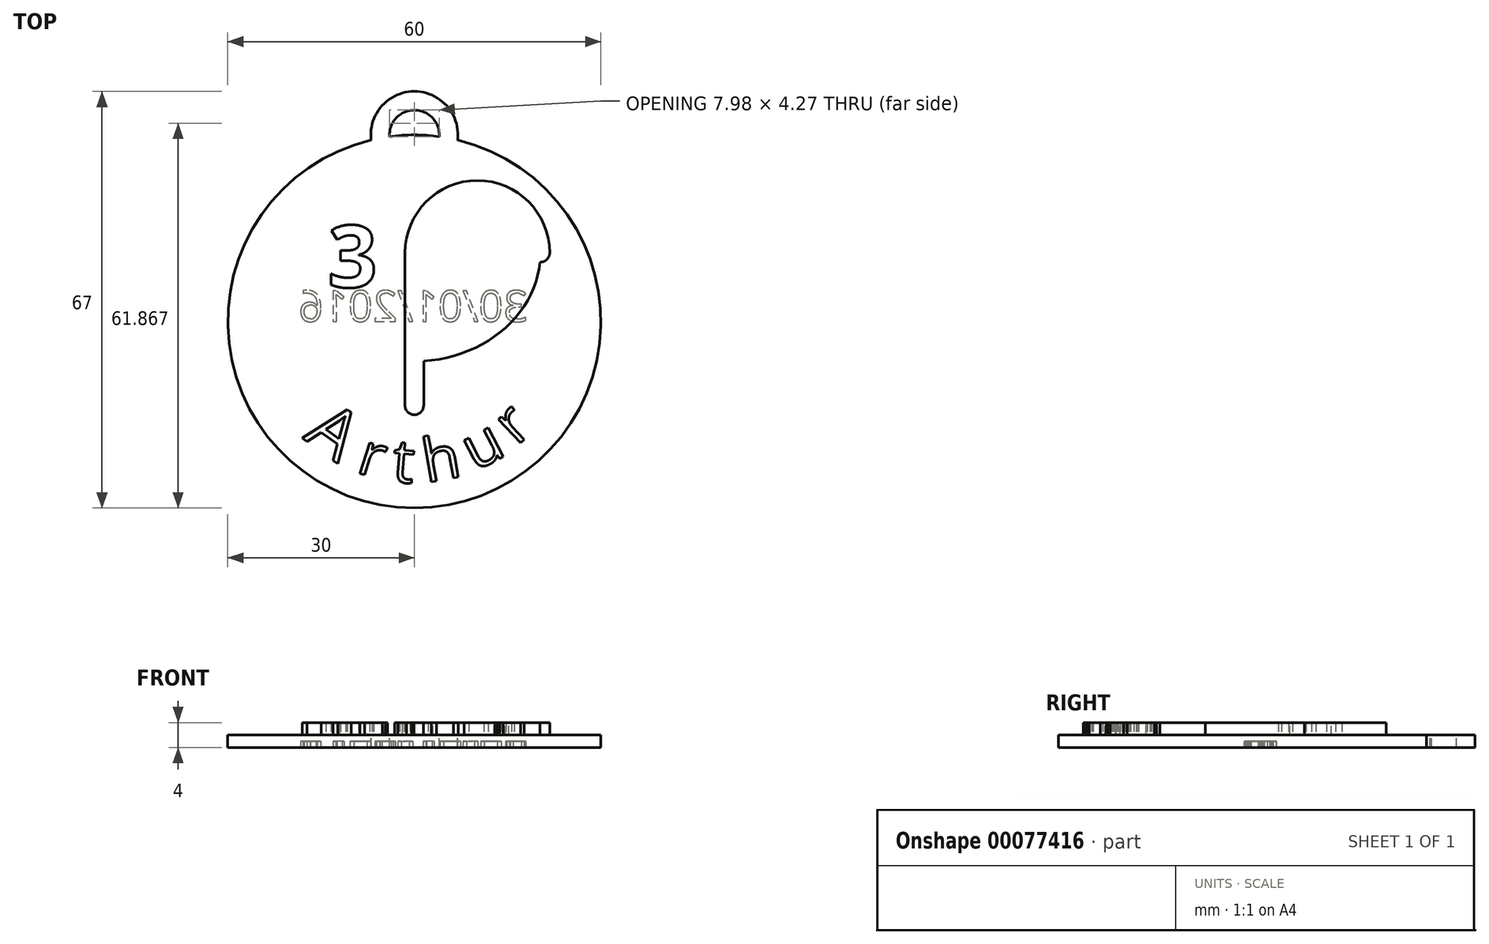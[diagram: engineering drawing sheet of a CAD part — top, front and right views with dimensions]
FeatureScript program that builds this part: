
annotation { "Feature Type Name" : "Feature", "Feature Type Description" : "" }
export const myFeature = defineFeature(function(context is Context, id is Id, definition is map)
    precondition{}
    {
        {
            var Q0;
            Q0=qCreatedBy(makeId("Top.planeOp"),FACE);
            var sketch = newSketch(context, id + "F0", { "sketchPlane" : qUnion([Q0])});
            skCircle(sketch, "E0", {"center": v(0, 0) * mm, "radius": 30 * mm});
            skSolve(sketch);
        }
        {
            var Q0;
            Q0=qSketchRegion(id+"F0",true);
            extrude(context, id + "F1", {"entities" : qUnion([Q0]), "oppositeDirection" : true, "depth" : 2 * mm});
        }
        {
            var Q0;
            Q0=qCreatedBy(makeId("Top.planeOp"),FACE);
            var sketch = newSketch(context, id + "F2", { "sketchPlane" : qUnion([Q0])});
            skEllipticalArc(sketch, "E1", {});
            skLineSegment(sketch, "E2", {"start": v(0, 0) * mm, "end": v(0, 30) * mm, "construction": true});
            skLineSegment(sketch, "E3", {"start": v(0, 11.04) * mm, "end": v(0, -13.5) * mm});
            skArc(sketch, "E4", {"start": v(20.27, 11.04) * mm, "mid": v(10.13, 21.17) * mm, "end": v(0, 11.04) * mm});
            skLineSegment(sketch, "E5", {"start": v(0, 11.04) * mm, "end": v(-16.84, 20.76) * mm, "construction": true});
            skLineSegment(sketch, "E6", {"start": v(0, 11.04) * mm, "end": v(-20.27, 11.04) * mm, "construction": true});
            skArc(sketch, "E7.0.startCap", {"start": v(-1.5, 11.04) * mm, "mid": v(0, 12.54) * mm, "end": v(1.5, 11.04) * mm});
            skArc(sketch, "E7.0.endCap", {"start": v(1.5, -13.5) * mm, "mid": v(0, -15) * mm, "end": v(-1.5, -13.5) * mm});
            skLineSegment(sketch, "E7.0.left", {"start": v(1.5, 11.04) * mm, "end": v(1.5, -13.5) * mm});
            skLineSegment(sketch, "E7.0.right", {"start": v(-1.5, 11.04) * mm, "end": v(-1.5, -13.5) * mm});
            skArc(sketch, "E8.0.startCap", {"start": v(21.77, 11.04) * mm, "mid": v(20.27, 9.54) * mm, "end": v(18.77, 11.04) * mm});
            skArc(sketch, "E8.0.endCap", {"start": v(1.5, 11.04) * mm, "mid": v(0, 9.54) * mm, "end": v(-1.5, 11.04) * mm});
            skArc(sketch, "E8.0.left", {"start": v(18.77, 11.04) * mm, "mid": v(10.13, 19.67) * mm, "end": v(1.5, 11.04) * mm});
            skArc(sketch, "E8.0.right", {"start": v(21.77, 11.04) * mm, "mid": v(10.13, 22.67) * mm, "end": v(-1.5, 11.04) * mm});
            skArc(sketch, "E8.1.startCap", {"start": v(-18.02, 21.68) * mm, "mid": v(-15.91, 21.95) * mm, "end": v(-15.65, 19.84) * mm});
            skArc(sketch, "E8.1.endCap", {"start": v(18.77, 11.04) * mm, "mid": v(20.27, 12.54) * mm, "end": v(21.77, 11.04) * mm});
            skFitSpline(sketch, "E8.1.left", {"points": [v(18.7, 9.5) * mm, v(18.8, 11.04) * mm, v(18.7, 12.6) * mm, v(18.36, 14.63) * mm, v(17.66, 16.6) * mm, v(16.63, 18.49) * mm, v(15.37, 20.3) * mm, v(13.44, 22.32) * mm, v(11.07, 24) * mm, v(8.94, 25.1) * mm, v(6.7, 26.01) * mm, v(4.32, 26.63) * mm, v(1.87, 26.95) * mm, v(0, 27.03) * mm, v(-1.87, 26.95) * mm, v(-4.32, 26.63) * mm, v(-6.7, 26.01) * mm, v(-8.94, 25.1) * mm, v(-11.07, 24) * mm, v(-13.44, 22.32) * mm, v(-15.37, 20.3) * mm, v(-16.63, 18.49) * mm, v(-17.66, 16.6) * mm, v(-18.36, 14.63) * mm, v(-18.7, 12.6) * mm, v(-18.8, 11.04) * mm, v(-18.7, 9.5) * mm, v(-18.36, 7.46) * mm, v(-17.66, 5.48) * mm, v(-16.63, 3.6) * mm, v(-15.37, 1.8) * mm, v(-13.44, -0.24) * mm, v(-11.07, -1.92) * mm, v(-8.94, -3.02) * mm, v(-6.7, -3.93) * mm, v(-4.32, -4.55) * mm, v(-1.87, -4.86) * mm, v(0, -4.94) * mm, v(1.87, -4.86) * mm, v(4.32, -4.55) * mm, v(6.7, -3.93) * mm, v(8.94, -3.02) * mm, v(11.07, -1.92) * mm, v(13.44, -0.24) * mm, v(15.37, 1.8) * mm, v(16.63, 3.6) * mm, v(17.66, 5.48) * mm, v(18.36, 7.46) * mm, v(18.7, 9.5) * mm, v(18.8, 11.04) * mm, v(18.7, 12.6) * mm]});
            skFitSpline(sketch, "E8.1.right", {"points": [v(21.7, 9.15) * mm, v(21.8, 11.04) * mm, v(21.7, 12.93) * mm, v(21.27, 15.42) * mm, v(20.42, 17.81) * mm, v(19.18, 20.07) * mm, v(17.69, 22.22) * mm, v(15.4, 24.61) * mm, v(12.65, 26.56) * mm, v(10.2, 27.83) * mm, v(7.62, 28.88) * mm, v(4.92, 29.58) * mm, v(2.12, 29.94) * mm, v(0, 30.03) * mm, v(-2.12, 29.94) * mm, v(-4.92, 29.58) * mm, v(-7.62, 28.88) * mm, v(-10.2, 27.83) * mm, v(-12.65, 26.56) * mm, v(-15.4, 24.61) * mm, v(-17.69, 22.22) * mm, v(-19.18, 20.07) * mm, v(-20.42, 17.81) * mm, v(-21.27, 15.42) * mm, v(-21.7, 12.93) * mm, v(-21.8, 11.04) * mm, v(-21.7, 9.15) * mm, v(-21.27, 6.67) * mm, v(-20.42, 4.27) * mm, v(-19.18, 2) * mm, v(-17.69, -0.14) * mm, v(-15.4, -2.53) * mm, v(-12.65, -4.48) * mm, v(-10.2, -5.75) * mm, v(-7.62, -6.8) * mm, v(-4.92, -7.5) * mm, v(-2.12, -7.86) * mm, v(0, -7.95) * mm, v(2.12, -7.86) * mm, v(4.92, -7.5) * mm, v(7.62, -6.8) * mm, v(10.2, -5.75) * mm, v(12.65, -4.48) * mm, v(15.4, -2.53) * mm, v(17.69, -0.14) * mm, v(19.18, 2) * mm, v(20.42, 4.27) * mm, v(21.27, 6.67) * mm, v(21.7, 9.15) * mm, v(21.8, 11.04) * mm, v(21.7, 12.93) * mm]});
            const initialGuessF2  = {"E1": [0, 0.011041626236194823, 1, 0, 0.020266667008310185, 0.017458373763805178, 2.5511335140588507, 0]};
            skSetInitialGuess(sketch, initialGuessF2);
            skSolve(sketch);
        }
        {
            var Q0;
            {var subQ0=sQuery(id+"F2.wireOp",EDGE,"E8.1.startCap");Q0=makeQuery(id+"F2.imprint","IMPRINT",FACE,{"disambiguationData":[TD([[makeQuery(id+"F2.imprint","IMPRINT",EDGE,{"derivedFrom":subQ0}),-1.0]])]});}
            var Q1;
            {var subQ0=sQuery(id+"F2.wireOp",EDGE,"E7.0.right");var subQ1=sQuery(id+"F2.wireOp",EDGE,"E1");var subQ2=makeQuery(id+"F2.imprint","INTERSECT",VERTEX,{"derivedFrom":[subQ1,subQ0]});Q1=makeQuery(id+"F2.imprint","IMPRINT",FACE,{"disambiguationData":[TD([[makeQuery(id+"F2.imprint","IMPRINT",EDGE,{"disambiguationData":[TD([[subQ2,-1.0]])],"derivedFrom":subQ1}),1.0]])]});}
            var Q2;
            {var subQ0=sQuery(id+"F2.wireOp",EDGE,"E3");var subQ1=sQuery(id+"F2.wireOp",EDGE,"E1");var subQ2=makeQuery(id+"F2.imprint","INTERSECT",VERTEX,{"derivedFrom":[subQ1,subQ0]});Q2=makeQuery(id+"F2.imprint","IMPRINT",FACE,{"disambiguationData":[TD([[makeQuery(id+"F2.imprint","IMPRINT",EDGE,{"disambiguationData":[TD([[subQ2,-1.0]])],"derivedFrom":subQ1}),1.0]])]});}
            var Q3;
            {var subQ0=sQuery(id+"F2.wireOp",EDGE,"E7.0.right");var subQ1=sQuery(id+"F2.wireOp",EDGE,"E1");var subQ2=makeQuery(id+"F2.imprint","INTERSECT",VERTEX,{"derivedFrom":[subQ1,subQ0]});Q3=makeQuery(id+"F2.imprint","IMPRINT",FACE,{"disambiguationData":[TD([[makeQuery(id+"F2.imprint","IMPRINT",EDGE,{"disambiguationData":[TD([[subQ2,-1.0]])],"derivedFrom":subQ1}),-1.0]])]});}
            var Q4;
            {var subQ0=sQuery(id+"F2.wireOp",EDGE,"E3");var subQ1=sQuery(id+"F2.wireOp",EDGE,"E1");var subQ2=makeQuery(id+"F2.imprint","INTERSECT",VERTEX,{"derivedFrom":[subQ1,subQ0]});Q4=makeQuery(id+"F2.imprint","IMPRINT",FACE,{"disambiguationData":[TD([[makeQuery(id+"F2.imprint","IMPRINT",EDGE,{"disambiguationData":[TD([[subQ2,-1.0]])],"derivedFrom":subQ1}),-1.0]])]});}
            var Q5;
            {var subQ0=sQuery(id+"F2.wireOp",EDGE,"E7.0.left");var subQ1=sQuery(id+"F2.wireOp",EDGE,"E1");var subQ2=makeQuery(id+"F2.imprint","INTERSECT",VERTEX,{"derivedFrom":[subQ1,subQ0]});Q5=makeQuery(id+"F2.imprint","IMPRINT",FACE,{"disambiguationData":[TD([[makeQuery(id+"F2.imprint","IMPRINT",EDGE,{"disambiguationData":[TD([[subQ2,-1.0]])],"derivedFrom":subQ1}),-1.0]])]});}
            var Q6;
            {var subQ0=sQuery(id+"F2.wireOp",EDGE,"E7.0.left");var subQ1=sQuery(id+"F2.wireOp",EDGE,"E1");var subQ2=makeQuery(id+"F2.imprint","INTERSECT",VERTEX,{"derivedFrom":[subQ1,subQ0]});Q6=makeQuery(id+"F2.imprint","IMPRINT",FACE,{"disambiguationData":[TD([[makeQuery(id+"F2.imprint","IMPRINT",EDGE,{"disambiguationData":[TD([[subQ2,-1.0]])],"derivedFrom":subQ1}),1.0]])]});}
            var Q7;
            {var subQ0=sQuery(id+"F2.wireOp",EDGE,"E4");var subQ1=sQuery(id+"F2.wireOp",EDGE,"E1");var subQ2=makeQuery(id+"F2.imprint","INTERSECT",VERTEX,{"derivedFrom":[subQ1,subQ0]});Q7=makeQuery(id+"F2.imprint","IMPRINT",FACE,{"disambiguationData":[TD([[makeQuery(id+"F2.imprint","IMPRINT",EDGE,{"disambiguationData":[TD([[subQ2,1.0]])],"derivedFrom":subQ1}),-1.0]])]});}
            var Q8;
            {var subQ0=sQuery(id+"F2.wireOp",EDGE,"E4");var subQ1=sQuery(id+"F2.wireOp",EDGE,"E1");var subQ2=makeQuery(id+"F2.imprint","INTERSECT",VERTEX,{"derivedFrom":[subQ1,subQ0]});Q8=makeQuery(id+"F2.imprint","IMPRINT",FACE,{"disambiguationData":[TD([[makeQuery(id+"F2.imprint","IMPRINT",EDGE,{"disambiguationData":[TD([[subQ2,1.0]])],"derivedFrom":subQ1}),1.0]])]});}
            var Q9;
            {var subQ5=sQuery(id+"F2.wireOp",EDGE,"E8.0.left");Q9=makeQuery(id+"F2.imprint","IMPRINT",FACE,{"disambiguationData":[TD([[makeQuery(id+"F2.imprint","IMPRINT",EDGE,{"derivedFrom":subQ5}),-1.0]])]});}
            var Q10;
            {var subQ5=sQuery(id+"F2.wireOp",EDGE,"E8.0.right");Q10=makeQuery(id+"F2.imprint","IMPRINT",FACE,{"disambiguationData":[TD([[makeQuery(id+"F2.imprint","IMPRINT",EDGE,{"derivedFrom":subQ5}),1.0]])]});}
            var Q11;
            {var subQ0=sQuery(id+"F2.wireOp",EDGE,"E4");var subQ1=sQuery(id+"F2.wireOp",EDGE,"E3");var subQ2=makeQuery(id+"F2.imprint","INTERSECT",VERTEX,{"derivedFrom":[subQ1,subQ0]});Q11=makeQuery(id+"F2.imprint","IMPRINT",FACE,{"disambiguationData":[TD([[makeQuery(id+"F2.imprint","IMPRINT",EDGE,{"disambiguationData":[TD([[subQ2,-1.0]])],"derivedFrom":subQ1}),-1.0]])]});}
            var Q12;
            {var subQ0=sQuery(id+"F2.wireOp",EDGE,"E4");var subQ1=sQuery(id+"F2.wireOp",EDGE,"E3");var subQ2=makeQuery(id+"F2.imprint","INTERSECT",VERTEX,{"derivedFrom":[subQ1,subQ0]});Q12=makeQuery(id+"F2.imprint","IMPRINT",FACE,{"disambiguationData":[TD([[makeQuery(id+"F2.imprint","IMPRINT",EDGE,{"disambiguationData":[TD([[subQ2,-1.0]])],"derivedFrom":subQ1}),1.0]])]});}
            var Q13;
            {var subQ0=sQuery(id+"F2.wireOp",EDGE,"E8.0.endCap");var subQ1=sQuery(id+"F2.wireOp",EDGE,"E3");var subQ2=makeQuery(id+"F2.imprint","INTERSECT",VERTEX,{"derivedFrom":[subQ1,subQ0]});Q13=makeQuery(id+"F2.imprint","IMPRINT",FACE,{"disambiguationData":[TD([[makeQuery(id+"F2.imprint","IMPRINT",EDGE,{"disambiguationData":[TD([[subQ2,-1.0]])],"derivedFrom":subQ1}),-1.0]])]});}
            var Q14;
            {var subQ0=sQuery(id+"F2.wireOp",EDGE,"E8.0.endCap");var subQ1=sQuery(id+"F2.wireOp",EDGE,"E3");var subQ2=makeQuery(id+"F2.imprint","INTERSECT",VERTEX,{"derivedFrom":[subQ1,subQ0]});Q14=makeQuery(id+"F2.imprint","IMPRINT",FACE,{"disambiguationData":[TD([[makeQuery(id+"F2.imprint","IMPRINT",EDGE,{"disambiguationData":[TD([[subQ2,-1.0]])],"derivedFrom":subQ1}),1.0]])]});}
            var Q15;
            {var subQ1=sQuery(id+"F2.wireOp",EDGE,"E7.0.endCap");Q15=makeQuery(id+"F2.imprint","IMPRINT",FACE,{"disambiguationData":[TD([[makeQuery(id+"F2.imprint","IMPRINT",EDGE,{"derivedFrom":subQ1}),-1.0]])]});}
            extrude(context, id + "F3", {"entities" : qUnion([Q0, Q1, Q2, Q3, Q4, Q5, Q6, Q7, Q8, Q9, Q10, Q11, Q12, Q13, Q14, Q15]), "operationType" : NewBodyOperationType.ADD, "depth" : 2 * mm});
        }
        {
            var Q0;
            Q0=qCreatedBy(makeId("Top.planeOp"),FACE);
            var sketch = newSketch(context, id + "F4", { "sketchPlane" : qUnion([Q0])});
            skText(sketch, "E9", { "text": "3", "fontName": "OpenSans-Bold.ttf"});
            skText(sketch, "E10", { "text": "D", "fontName": "OpenSans-Bold.ttf"});
            const initialGuessF4  = {"E9": [-0.0139, 0.0055, 1, 0, 0.01], "E10": [0.0055, 0.0055, 1, 0, 0.01]};
            skSetInitialGuess(sketch, initialGuessF4);
            skSolve(sketch);
        }
        {
            var Q0;
            Q0=qSketchRegion(id+"F4",true);
            extrude(context, id + "F5", {"entities" : qUnion([Q0]), "operationType" : NewBodyOperationType.ADD, "depth" : 2 * mm});
        }
        {
            var Q0;
            {var subQ8=sQuery(id+"F0.wireOp",EDGE,"E0");Q0=makeQuery(id+"F3.boolean.opBoolean","SPLIT",FACE,{"disambiguationData":[TD([makeQuery(id+"F1.opExtrude","SWEPT_FACE",FACE,{"disambiguationData":[OSD([subQ8])]})])],"derivedFrom":makeQuery(id+"F1.opExtrude","CAP_FACE",FACE,{"disambiguationData":[OSD([subQ8])],"isStart":true})});}
            var sketch = newSketch(context, id + "F6", { "sketchPlane" : qUnion([Q0])});
            skCircle(sketch, "E11.0", {"center": v(0, 0) * mm, "radius": 26 * mm, "construction": true});
            skText(sketch, "E12", { "text": "A", "fontName": "OpenSans-Regular.ttf"});
            skText(sketch, "E13", { "text": "r", "fontName": "OpenSans-Regular.ttf"});
            skText(sketch, "E14", { "text": "t", "fontName": "OpenSans-Regular.ttf"});
            skText(sketch, "E15", { "text": "h", "fontName": "OpenSans-Regular.ttf"});
            skText(sketch, "E16", { "text": "u", "fontName": "OpenSans-Regular.ttf"});
            skText(sketch, "E17", { "text": "r", "fontName": "OpenSans-Regular.ttf"});
            const initialGuessF6  = {"E12": [-0.018, -0.01876, 0.80851, -0.58848, 0.008], "E13": [-0.00954, -0.02419, 0.95474, -0.29746, 0.007], "E14": [-0.00368, -0.02574, 0.9968, -0.07986, 0.007], "E15": [0.00194, -0.02593, 0.9848, 0.17368, 0.007], "E16": [0.00977, -0.0241, 0.88503, 0.46553, 0.007], "E17": [0.0165, -0.02009, 0.72376, 0.69006, 0.007]};
            skSetInitialGuess(sketch, initialGuessF6);
            skSolve(sketch);
        }
        {
            var Q0;
            Q0=qSketchRegion(id+"F6",true);
            extrude(context, id + "F7", {"entities" : qUnion([Q0]), "operationType" : NewBodyOperationType.ADD, "depth" : 2 * mm});
        }
        {
            var Q0;
            Q0=qCreatedBy(makeId("Top.planeOp"),FACE);
            var sketch = newSketch(context, id + "F8", { "sketchPlane" : qUnion([Q0])});
            skArc(sketch, "E18", {"start": v(5.48, 29.5) * mm, "mid": v(0, 35.5) * mm, "end": v(-5.48, 29.5) * mm});
            skArc(sketch, "E19.0.startCap", {"start": v(6.97, 29.36) * mm, "mid": v(5.34, 28) * mm, "end": v(3.98, 29.63) * mm});
            skArc(sketch, "E19.0.endCap", {"start": v(-3.98, 29.63) * mm, "mid": v(-5.34, 28) * mm, "end": v(-6.97, 29.36) * mm});
            skArc(sketch, "E19.0.left", {"start": v(3.98, 29.63) * mm, "mid": v(0, 34) * mm, "end": v(-3.98, 29.63) * mm});
            skArc(sketch, "E19.0.right", {"start": v(6.97, 29.36) * mm, "mid": v(0, 37) * mm, "end": v(-6.97, 29.36) * mm});
            skSolve(sketch);
        }
        {
            var Q0;
            Q0=qSketchRegion(id+"F8",true);
            extrude(context, id + "F9", {"entities" : qUnion([Q0]), "operationType" : NewBodyOperationType.ADD, "oppositeDirection" : true, "depth" : 2 * mm});
        }
        {
            var Q0;
            Q0=makeQuery(id+"F9.boolean.opBoolean","MERGE",FACE,{"derivedFrom":[makeQuery(id+"F1.opExtrude","CAP_FACE",FACE,{"disambiguationData":[OSD([sQuery(id+"F0.wireOp",EDGE,"E0")])],"isStart":false}),makeQuery(id+"F9.opExtrude","CAP_FACE",FACE,{"disambiguationData":[OSD([sQuery(id+"F8.wireOp",EDGE,"E19.0.startCap"),sQuery(id+"F8.wireOp",EDGE,"E19.0.endCap"),sQuery(id+"F8.wireOp",EDGE,"E19.0.left"),sQuery(id+"F8.wireOp",EDGE,"E19.0.right")])],"isStart":false})]});
            var sketch = newSketch(context, id + "F10", { "sketchPlane" : qUnion([Q0])});
            skText(sketch, "E20", { "text": "30/01/2016", "fontName": "OpenSans-Regular.ttf"});
            const initialGuessF10  = {"E20": [0.01826, 0, -1, 0, 0.005]};
            skSetInitialGuess(sketch, initialGuessF10);
            skSolve(sketch);
        }
        {
            var Q0;
            Q0=qSketchRegion(id+"F10",true);
            extrude(context, id + "F11", {"entities" : qUnion([Q0]), "operationType" : NewBodyOperationType.REMOVE, "oppositeDirection" : true, "depth" : 1 * mm});
        }
    });
